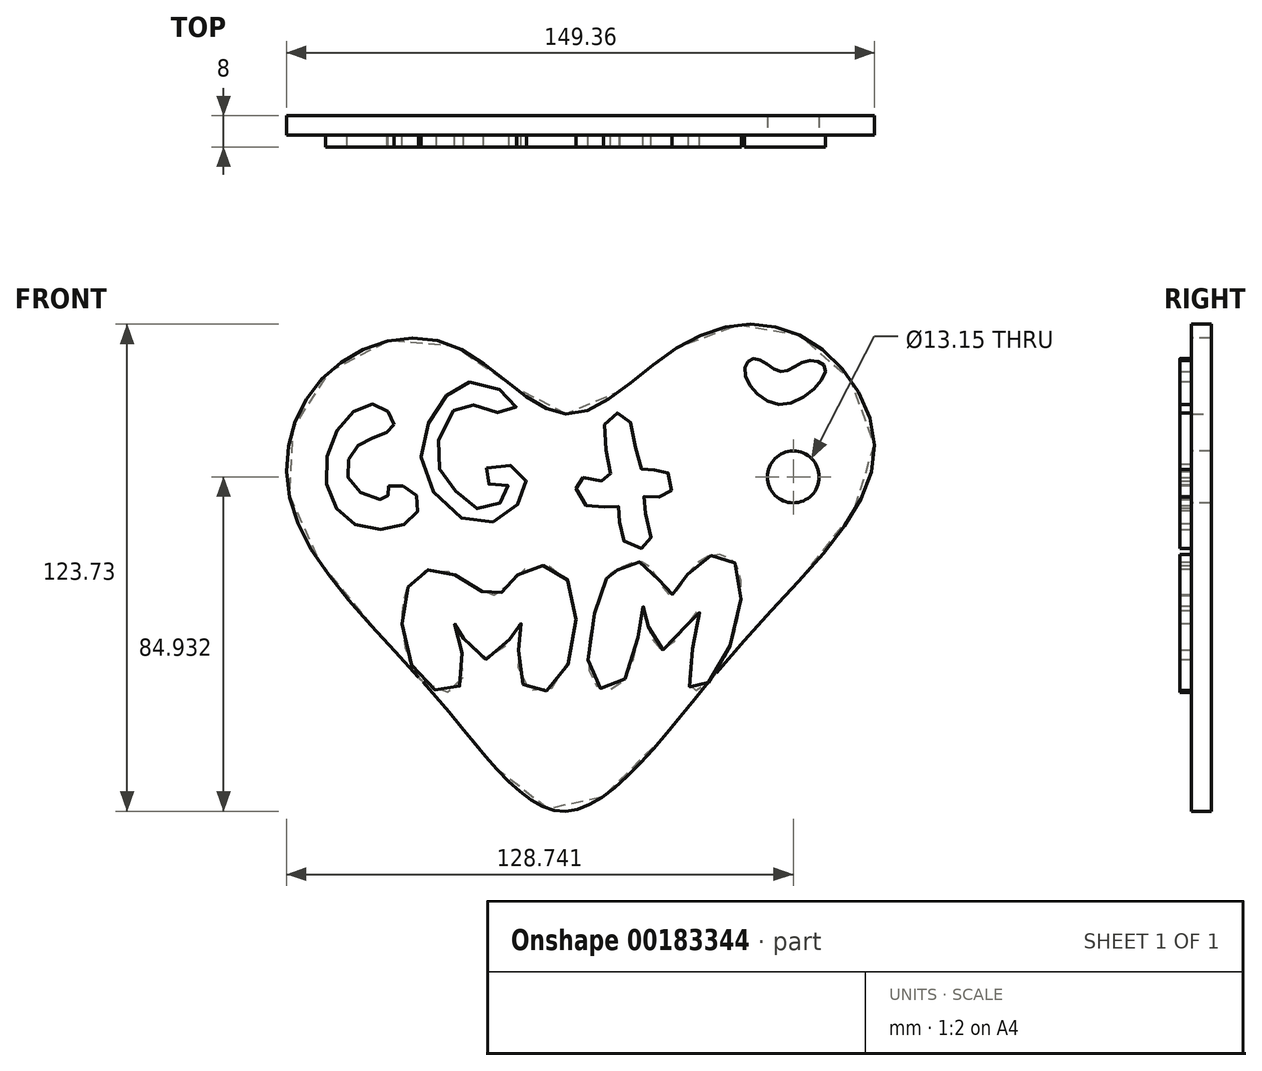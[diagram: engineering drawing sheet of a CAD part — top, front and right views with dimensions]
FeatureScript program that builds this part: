
annotation { "Feature Type Name" : "Feature", "Feature Type Description" : "" }
export const myFeature = defineFeature(function(context is Context, id is Id, definition is map)
    precondition{}
    {
        {
            var Q0;
            Q0=qCreatedBy(makeId("Front.planeOp"),FACE);
            var sketch = newSketch(context, id + "F0", { "sketchPlane" : qUnion([Q0])});
            skFitSpline(sketch, "E0", {"points": [v(0, 37.91) * mm, v(-29.95, 55.72) * mm, v(-62.07, 46.82) * mm, v(-69.35, 13.36) * mm, v(-32.65, -34.4) * mm, v(0, -63) * mm, v(42.9, -22.26) * mm, v(78.26, 27.39) * mm, v(59.9, 57.61) * mm, v(28.87, 55.18) * mm, v(0, 37.91) * mm]});
            skSolve(sketch);
        }
        {
            var Q0;
            Q0 = qSketchRegion(id + "F0", true);
            extrude(context, id + "F1", {"entities" : qUnion([Q0]), "depth" : 5 * mm});
        }
        {
            var Q0;
            Q0=makeQuery(id+"F1.opExtrude","CAP_FACE",FACE,{"disambiguationData":[OSD([sQuery(id+"F0.wireOp",EDGE,"E0")])],"isStart":false});
            var sketch = newSketch(context, id + "F2", { "sketchPlane" : qUnion([Q0])});
            skFitSpline(sketch, "E1", {"points": [v(-43.72, 35.22) * mm, v(-48.57, 40.34) * mm, v(-60.18, 29.55) * mm, v(-55.05, 10.66) * mm, v(-38.86, 11.47) * mm, v(-39.13, 18.48) * mm, v(-45.33, 19.3) * mm, v(-45.33, 16.6) * mm, v(-53.97, 19.3) * mm, v(-54.24, 28.47) * mm, v(-47.22, 32.52) * mm, v(-43.72, 35.22) * mm]});
            skFitSpline(sketch, "E2", {"points": [v(-20.24, 24.15) * mm, v(-11.6, 23.61) * mm, v(-11.33, 16.33) * mm, v(-22.67, 10.12) * mm, v(-36.43, 24.15) * mm, v(-31.84, 40.88) * mm, v(-22.13, 46) * mm, v(-12.68, 39.8) * mm, v(-18.89, 38.45) * mm, v(-26.45, 40.34) * mm, v(-32.92, 27.93) * mm, v(-28.06, 18.21) * mm, v(-19.43, 13.63) * mm, v(-14.57, 19.56) * mm, v(-19.7, 20.1) * mm, v(-20.24, 24.15) * mm]});
            skFitSpline(sketch, "E3", {"points": [v(9.71, 35.22) * mm, v(10.8, 21.18) * mm, v(3.24, 21.45) * mm, v(5.4, 14.44) * mm, v(13.22, 14.44) * mm, v(14.3, 6.07) * mm, v(21.32, 5) * mm, v(19.7, 16.87) * mm, v(25.9, 17.14) * mm, v(25.1, 23.61) * mm, v(19.43, 23.61) * mm, v(15.38, 37.37) * mm, v(9.71, 35.22) * mm]});
            skFitSpline(sketch, "E4", {"points": [v(-40.2, -6.07) * mm, v(-36.38, -30.16) * mm, v(-26.45, -30.09) * mm, v(-28.33, -15.25) * mm, v(-20.24, -24.42) * mm, v(-11.6, -15.25) * mm, v(-11.6, -29.55) * mm, v(-2.7, -30.9) * mm, v(0, -3.64) * mm, v(-11.6, -2.3) * mm, v(-18.08, -8.23) * mm, v(-30.5, -2.02) * mm, v(-40.2, -6.07) * mm]});
            skFitSpline(sketch, "E5", {"points": [v(10.25, -3.91) * mm, v(6.48, -29.55) * mm, v(14.84, -29.55) * mm, v(19.7, -10.93) * mm, v(24.02, -22) * mm, v(33.73, -12) * mm, v(31.3, -31.17) * mm, v(38.14, -27.88) * mm, v(42.9, 0) * mm, v(33.2, 0) * mm, v(26.45, -7.96) * mm, v(19.97, 0) * mm, v(12.41, -2.02) * mm, v(10.25, -3.91) * mm]});
            skFitSpline(sketch, "E6", {"points": [v(54.5, 48.7) * mm, v(61.26, 51.4) * mm, v(65.84, 49.25) * mm, v(54.5, 40.34) * mm, v(45.33, 48.98) * mm, v(48.3, 51.95) * mm, v(54.5, 48.7) * mm]});
            skSolve(sketch);
        }
        {
            var Q0;
            Q0 = qSketchRegion(id + "F2", true);
            extrude(context, id + "F3", {"entities" : qUnion([Q0]), "operationType" : NewBodyOperationType.ADD, "depth" : 3 * mm});
        }
        {
            var Q0;
            Q0=makeQuery(id+"F1.opExtrude","CAP_FACE",FACE,{"disambiguationData":[OSD([sQuery(id+"F0.wireOp",EDGE,"E0")])],"isStart":false});
            var sketch = newSketch(context, id + "F4", { "sketchPlane" : qUnion([Q0])});
            skCircle(sketch, "E7", {"center": v(57.7, 21.91) * mm, "radius": 6.58 * mm});
            skSolve(sketch);
        }
        {
            var Q0;
            Q0 = qSketchRegion(id + "F4", true);
            extrude(context, id + "F5", {"entities" : qUnion([Q0]), "operationType" : NewBodyOperationType.REMOVE, "oppositeDirection" : true, "depth" : 25 * mm});
        }
    });
